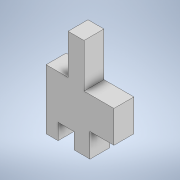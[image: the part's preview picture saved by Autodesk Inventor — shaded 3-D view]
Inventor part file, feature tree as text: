
AUTODESK INVENTOR PART (.ipt)
format: ipt  version: 2022 (Build 260153000, 153)  size: 114,688 bytes
history: native  units: mm
features: other x1, extrude x1, sketch x1
ambient origin geometry x8: Origin, YZ Plane, XZ Plane, XY Plane, X Axis, Y Axis, Z Axis, Center Point
bodies: Body1 (feature_tree)
feature tree (3):
  other  "Твердое тело1"
  extrude  "Выдавливание1"  Depth=8.0mm
  sketch  "Эскиз1"
